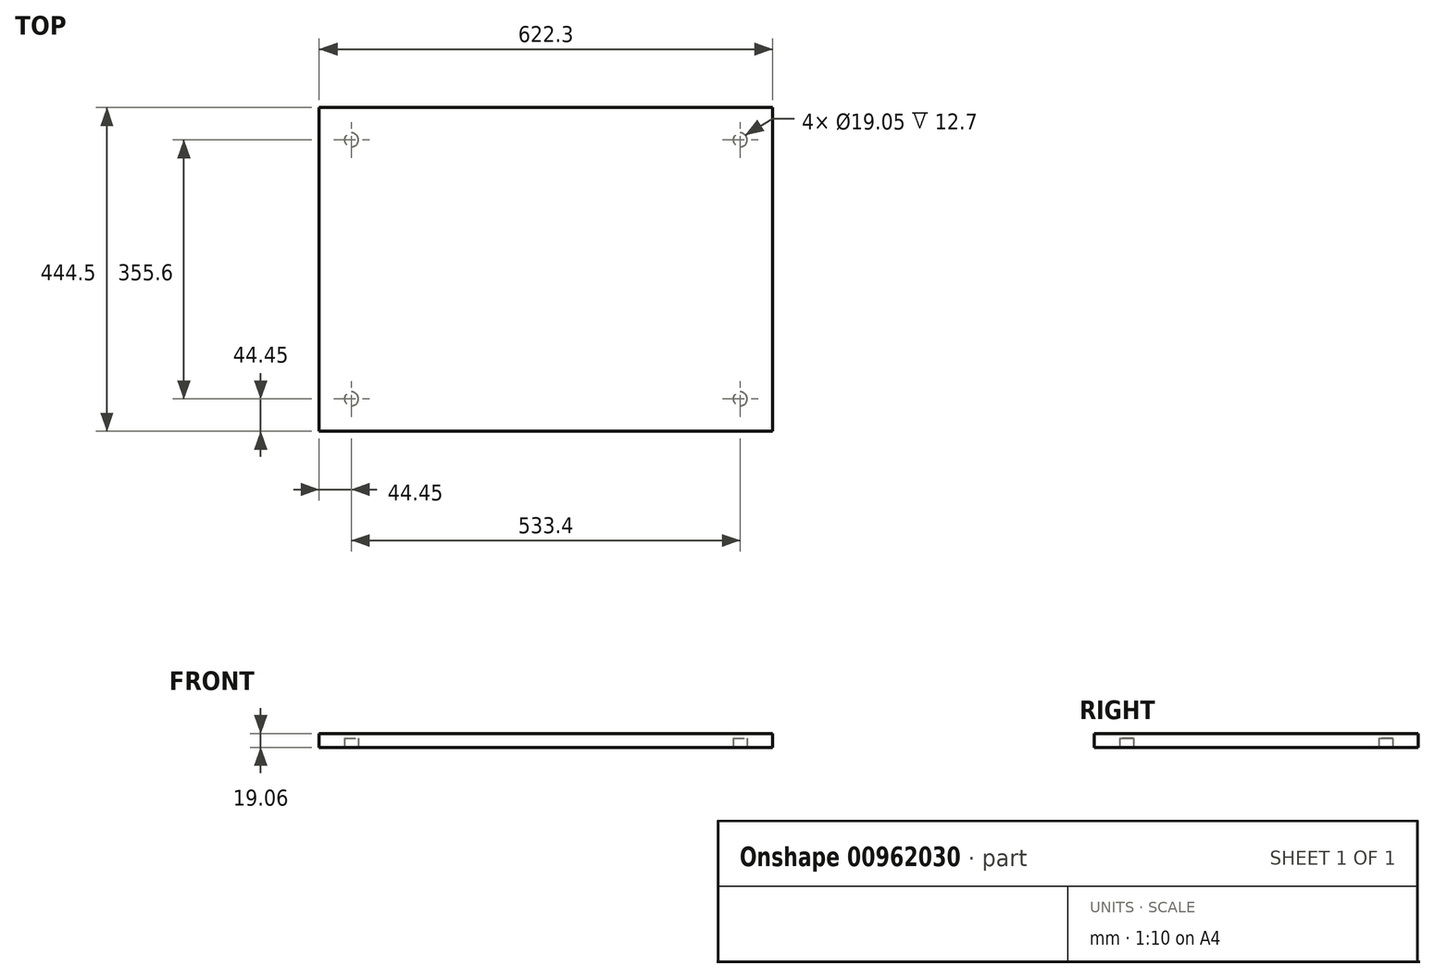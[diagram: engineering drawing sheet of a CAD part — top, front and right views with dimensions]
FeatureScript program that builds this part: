
annotation { "Feature Type Name" : "Feature", "Feature Type Description" : "" }
export const myFeature = defineFeature(function(context is Context, id is Id, definition is map)
    precondition{}
    {
        {
            var Q0;
            Q0=qCreatedBy(makeId("Top.planeOp"),FACE);
            var sketch = newSketch(context, id + "F0", { "sketchPlane" : qUnion([Q0])});
            skLineSegment(sketch, "E0.bottom", {"start": v(311.15, 222.25) * mm, "end": v(-311.15, 222.25) * mm});
            skLineSegment(sketch, "E0.top", {"start": v(311.15, -222.25) * mm, "end": v(-311.15, -222.25) * mm});
            skLineSegment(sketch, "E0.left", {"start": v(311.15, 222.25) * mm, "end": v(311.15, -222.25) * mm});
            skLineSegment(sketch, "E0.right", {"start": v(-311.15, 222.25) * mm, "end": v(-311.15, -222.25) * mm});
            skPoint(sketch, "E0.middle", {"position": v(0, 0) * mm});
            skSolve(sketch);
        }
        {
            var Q0;
            Q0=makeQuery(id+"F0.imprint","IMPRINT",FACE,{"disambiguationData":[TD([[makeQuery(id+"F0.imprint","IMPRINT",EDGE,{"derivedFrom":sQuery(id+"F0.wireOp",EDGE,"E0.bottom")}),1.0]])]});
            extrude(context, id + "F1", {"entities" : qUnion([Q0]), "endBound" : BoundingType.SYMMETRIC, "depth" : 19.05 * mm, "offsetDistance" : 25.4 * mm});
        }
        {
            var Q0;
            Q0=makeQuery(id+"F1.opExtrude","CAP_FACE",FACE,{"disambiguationData":[OSD([sQuery(id+"F0.wireOp",EDGE,"E0.bottom"),sQuery(id+"F0.wireOp",EDGE,"E0.top"),sQuery(id+"F0.wireOp",EDGE,"E0.left"),sQuery(id+"F0.wireOp",EDGE,"E0.right")])],"isStart":true});
            var sketch = newSketch(context, id + "F2", { "sketchPlane" : qUnion([Q0])});
            skLineSegment(sketch, "E1.bottom", {"start": v(266.7, 177.8) * mm, "end": v(-266.7, 177.8) * mm, "construction": true});
            skLineSegment(sketch, "E1.top", {"start": v(266.7, -177.8) * mm, "end": v(-266.7, -177.8) * mm, "construction": true});
            skLineSegment(sketch, "E1.left", {"start": v(266.7, 177.8) * mm, "end": v(266.7, -177.8) * mm, "construction": true});
            skLineSegment(sketch, "E1.right", {"start": v(-266.7, 177.8) * mm, "end": v(-266.7, -177.8) * mm, "construction": true});
            skPoint(sketch, "E1.middle", {"position": v(0, 0) * mm});
            skCircle(sketch, "E2", {"center": v(-266.7, 177.8) * mm, "radius": 9.53 * mm});
            skCircle(sketch, "E3", {"center": v(266.7, 177.8) * mm, "radius": 9.53 * mm});
            skCircle(sketch, "E4", {"center": v(266.7, -177.8) * mm, "radius": 9.52 * mm});
            skCircle(sketch, "E5", {"center": v(-266.7, -177.8) * mm, "radius": 9.52 * mm});
            skSolve(sketch);
        }
        {
            var Q0;
            Q0 = qSketchRegion(id + "F2", true);
            extrude(context, id + "F3", {"entities" : qUnion([Q0]), "operationType" : NewBodyOperationType.REMOVE, "oppositeDirection" : true, "depth" : 12.7 * mm, "offsetDistance" : 25.4 * mm});
        }
    });
